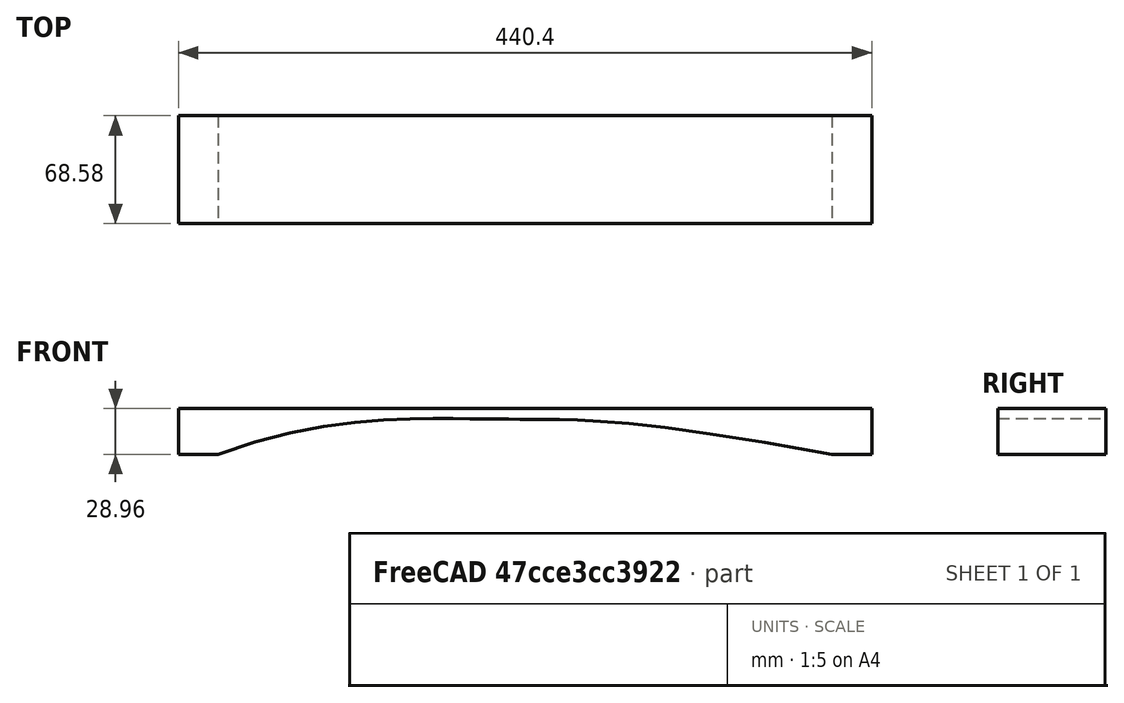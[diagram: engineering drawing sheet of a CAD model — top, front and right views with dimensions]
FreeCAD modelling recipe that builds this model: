
FCSTD DOCUMENT  (FreeCAD 0.20R29410 (Git))
Label: Single_Bar0
License: All rights reserved
LicenseURL: http://en.wikipedia.org/wiki/All_rights_reserved
objects: Sketcher::SketchObject×1, Part::Extrusion×1, Fem::FemSolverObjectPython×1, App::MaterialObjectPython×1, Fem::ConstraintDisplacement×1, Fem::FemMeshShapeNetgenObject×1, Fem::FemAnalysis×1
note: 2 computed .brp shape members not serialized (recipe doc carries the construction recipe); baked Part::Feature solids carry a one-line shape summary decoded from their .brp

FEATURE [Sketcher::SketchObject] Sketch
  FullyConstrained = true
  Placement = pos=(0,0,0) rot=(1,0,0;1.5708rad)
  sketch-geometry (12):
    g0: LineSegment StartX=25.29 StartY=0 StartZ=0 EndX=0 EndY=0 EndZ=0
    g1: LineSegment StartX=0 StartY=0 StartZ=0 EndX=0 EndY=28.96 EndZ=0
    g2: LineSegment StartX=0 StartY=28.96 StartZ=0 EndX=440.4 EndY=28.96 EndZ=0
    g3: LineSegment StartX=440.4 StartY=28.96 StartZ=0 EndX=440.4 EndY=0 EndZ=0
    g4: LineSegment StartX=440.4 StartY=0 StartZ=0 EndX=415.11 EndY=0 EndZ=0
    g5-g10: Circle x6 (B-spline internal-alignment scaffolding for g11; pole/knot coordinates omitted)
    g11: BSplineCurve PolesCount=6 KnotsCount=4 Degree=3 IsPeriodic=0
  constraints (38):
    c: DistanceX(g0) = 0
    c: DistanceY(g0) = 0
    c: Distance(g1,g1) = 28.96
    c: Distance(g2,g2) = 440.4
    c: DistanceX(g0,g0) = 25.29
    c: DistanceX(g4,g4) = 25.29
    c: Horizontal(g0)
    c: Vertical(g1)
    c: Horizontal(g2)
    c: Vertical(g3)
    c: Horizontal(g4)
    c: Equal(g3,g1)
    c: Coincident(g0,g1)
    c: Coincident(g1,g2)
    c: Coincident(g2,g3)
    c: Coincident(g3,g4)
    c: DistanceX(g6) = 296.03
    c: DistanceY(g6) = 21.75
    c: DistanceX(g7) = 222.34
    c: DistanceY(g7) = 21.99
    c: DistanceX(g8) = 191.75
    c: DistanceY(g8) = 22.68
    c: DistanceX(g9) = 86.07
    c: DistanceY(g9) = 22.85
    c: Weight(g5) = 1
    c: InternalAlignment(g5,g11)
    c: Weight(g6) = 1
    c: InternalAlignment(g6,g11)
    c: Weight(g7) = 1
    c: InternalAlignment(g7,g11)
    c: Weight(g8) = 1
    c: InternalAlignment(g8,g11)
    c: Weight(g9) = 1
    c: InternalAlignment(g9,g11)
    c: Weight(g10) = 1
    c: InternalAlignment(g10,g11)
    c: Coincident(g4,g11)
    c: Coincident(g0,g11)
FEATURE [Part::Extrusion] Bar
  Base = -> Sketch
  Dir = (0,-1,-3e-16)
  DirMode = 2
  FaceMakerClass = Part::FaceMakerBullseye
  LengthFwd = 68.58
  LengthRev = 0
  Solid = true
  Symmetric = false
FEATURE [Fem::FemSolverObjectPython] SolverCcxTools  # FEM object (typed FeaturePython)
  AnalysisType = 0
  BeamShellResultOutput3D = false
  BucklingFactors = 1
  EigenmodeHighLimit = 20000
  EigenmodeLowLimit = 20
  EigenmodesCount = 12
  GeometricalNonlinearity = 0
  IterationsControlParameterCutb = 0.25,0.5,0.75,0.85,,,1.5,
  IterationsControlParameterIter = 4,8,9,200,10,400,,200,,
  IterationsControlParameterTimeUse = false
  IterationsThermoMechMaximum = 2000
  IterationsUserDefinedIncrementations = false
  IterationsUserDefinedTimeStepLength = false
  MaterialNonlinearity = 0
  MatrixSolverType = 0
  SplitInputWriter = false
  ThermoMechSteadyState = false
  TimeEnd = 1
  TimeInitialStep = 0.01
FEATURE [App::MaterialObjectPython] MaterialSolid  # material (typed FeaturePython)
  Category = 0
  Material = CompressiveStrength=4300 kPa; Density=430 kg/m^3; Name=Wood-Chestnut; PoissonRatio=0.32; ShearModulus=7.4 MPa; UltimateTensileStrength=59.0 MPa; YoungsModulus=8500 MPa
FEATURE [Fem::ConstraintDisplacement] FemConstraintDisplacement
  NormalDirection = (0,3e-16,-1)
  Normals = (118) [(0,3.33067e-16,-1),(0,3.33067e-16,-1),(0,3.33067e-16,-1),(0,3.33067e-16,-1),(0,3.33067e-16,-1),(0,3.33067e-16,-1),(0,3.33067e-16,-1),+111 more]
  Points = (118) [(25.29,-68.58,-2.28417e-14),(16.86,-68.58,-2.28417e-14),(8.43,-68.58,-2.28417e-14),(0,-68.58,-2.28417e-14),(25.29,-45.72,-1.52278e-14),+113 more]
  References = -> [Bar]
  rotxFix = false
  rotxFree = true
  rotyFix = false
  rotyFree = true
  rotzFix = false
  rotzFree = true
  xDisplacement = 0
  xFix = false
  xFree = true
  xRotation = 0
  yDisplacement = 0
  yFix = true
  yFree = false
  yRotation = 0
  zDisplacement = 0
  zFix = false
  zFree = true
  zRotation = 0
FEATURE [Fem::FemMeshShapeNetgenObject] FEMMeshNetgen
  Fineness = 4
  GrowthRate = 0.3
  MaxSize = 10
  NbSegsPerEdge = 1
  NbSegsPerRadius = 2
  Optimize = true
  SecondOrder = true
  Shape = -> Bar
FEATURE [Fem::FemAnalysis] Analysis
  Group = -> [SolverCcxTools,MaterialSolid,FemConstraintDisplacement,FEMMeshNetgen]
